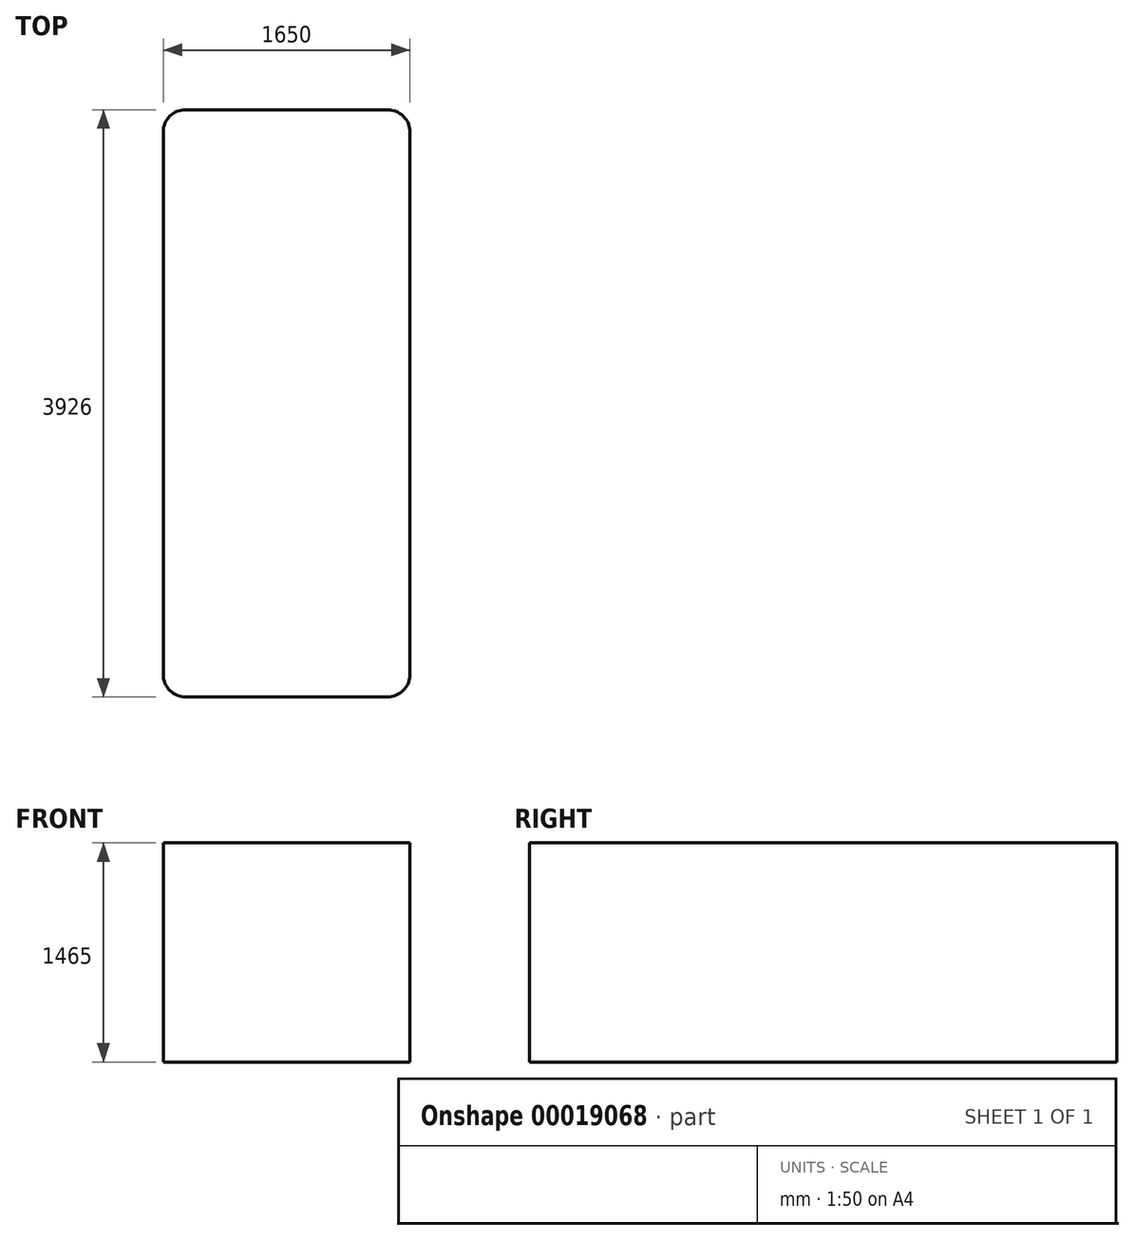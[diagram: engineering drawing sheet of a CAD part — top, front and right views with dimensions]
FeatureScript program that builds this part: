
annotation { "Feature Type Name" : "Feature", "Feature Type Description" : "" }
export const myFeature = defineFeature(function(context is Context, id is Id, definition is map)
    precondition{}
    {
        {
            var Q0;
            Q0=qCreatedBy(makeId("Top.planeOp"),FACE);
            var sketch = newSketch(context, id + "F0", { "sketchPlane" : qUnion([Q0])});
            skLineSegment(sketch, "E0.bottom", {"start": v(150, 0) * mm, "end": v(1500, 0) * mm});
            skLineSegment(sketch, "E0.top", {"start": v(150, 3926) * mm, "end": v(1500, 3926) * mm});
            skLineSegment(sketch, "E0.left", {"start": v(0, 150) * mm, "end": v(0, 3776) * mm});
            skLineSegment(sketch, "E0.right", {"start": v(1650, 150) * mm, "end": v(1650, 3776) * mm});
            skPoint(sketch, "E1.visualSharp", {"position": v(0, 3926) * mm});
            skArc(sketch, "E1.filletArc", {"start": v(150, 3926) * mm, "mid": v(43.93, 3882.07) * mm, "end": v(0, 3776) * mm});
            skPoint(sketch, "E2.visualSharp", {"position": v(1650, 3926) * mm});
            skArc(sketch, "E2.filletArc", {"start": v(1650, 3776) * mm, "mid": v(1606.07, 3882.07) * mm, "end": v(1500, 3926) * mm});
            skPoint(sketch, "E3.visualSharp", {"position": v(1650, 0) * mm});
            skArc(sketch, "E3.filletArc", {"start": v(1500, 0) * mm, "mid": v(1606.07, 43.93) * mm, "end": v(1650, 150) * mm});
            skPoint(sketch, "E4.visualSharp", {"position": v(0, 0) * mm});
            skArc(sketch, "E4.filletArc", {"start": v(0, 150) * mm, "mid": v(43.93, 43.93) * mm, "end": v(150, 0) * mm});
            skSolve(sketch);
        }
        {
            var Q0;
            Q0=makeQuery(id+"F0.imprint","IMPRINT",FACE,{"disambiguationData":[TD([[makeQuery(id+"F0.imprint","IMPRINT",EDGE,{"derivedFrom":sQuery(id+"F0.wireOp",EDGE,"E0.bottom")}),1.0]])]});
            extrude(context, id + "F1", {"entities" : qUnion([Q0]), "depth" : 1465 * mm});
        }
    });
